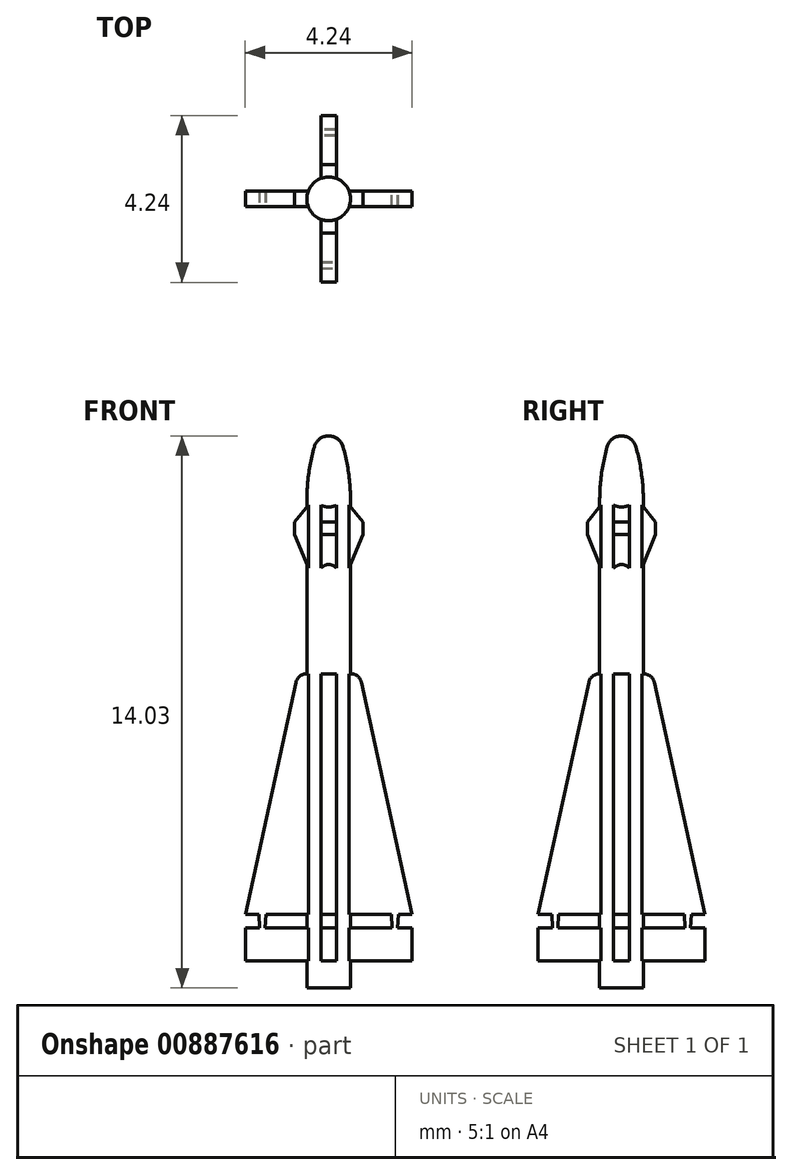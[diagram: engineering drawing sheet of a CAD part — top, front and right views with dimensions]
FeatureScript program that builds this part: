
annotation { "Feature Type Name" : "Feature", "Feature Type Description" : "" }
export const myFeature = defineFeature(function(context is Context, id is Id, definition is map)
    precondition{}
    {
        {
            var Q0;
            Q0=qCreatedBy(makeId("Front.planeOp"),FACE);
            var sketch = newSketch(context, id + "F0", { "sketchPlane" : qUnion([Q0])});
            skLineSegment(sketch, "E0", {"start": v(0, 0) * mm, "end": v(0, 14.03) * mm});
            skLineSegment(sketch, "E1", {"start": v(0.56, 12.36) * mm, "end": v(0.56, 0) * mm});
            skLineSegment(sketch, "E2", {"start": v(0.56, 0) * mm, "end": v(0, 0) * mm});
            skArc(sketch, "E3", {"start": v(0.37, 13.75) * mm, "mid": v(0.23, 13.95) * mm, "end": v(0, 14.03) * mm});
            skArc(sketch, "E4", {"start": v(0.56, 12.36) * mm, "mid": v(0.5, 13.06) * mm, "end": v(0.37, 13.75) * mm});
            skSolve(sketch);
        }
        {
            var Q0;
            {var subQ0=sQuery(id+"F0.wireOp",EDGE,"mrwio9nY-PsAZ-Zbfy-NhIU-sYq0QVbgGXAG");Q0=makeQuery(id+"F0.imprint","IMPRINT",FACE,{"disambiguationData":[TD([[makeQuery(id+"F0.imprint","IMPRINT",EDGE,{"derivedFrom":subQ0}),-1.0]])]});}
            var Q1;
            {var subQ7=sQuery(id+"F0.wireOp",EDGE,"E0");Q1=makeQuery(id+"F0.imprint","IMPRINT",FACE,{"disambiguationData":[TD([[makeQuery(id+"F0.imprint","IMPRINT",EDGE,{"derivedFrom":subQ7}),-1.0]])]});}
            var Q2;
            Q2=sQuery(id+"F0.wireOp",EDGE,"E0");
            revolve(context, id + "F1", {"surfaceOperationType" : NewSurfaceOperationType.NEW, "entities" : qUnion([Q0, Q1]), "axis" : qUnion([Q2]), "revolveType" : RevolveType.FULL});
        }
        {
            var Q0;
            Q0=qCreatedBy(makeId("Front.planeOp"),FACE);
            var sketch = newSketch(context, id + "F2", { "sketchPlane" : qUnion([Q0])});
            skLineSegment(sketch, "E5", {"start": v(0, 0) * mm, "end": v(0, 12.66) * mm});
            skLineSegment(sketch, "E6", {"start": v(0.4, 1.88) * mm, "end": v(0.4, 1.53) * mm});
            skLineSegment(sketch, "E7", {"start": v(0.4, 1.53) * mm, "end": v(2.12, 1.53) * mm});
            skLineSegment(sketch, "E8", {"start": v(0.56, 0) * mm, "end": v(0.56, 32.87) * mm, "construction": true});
            skLineSegment(sketch, "E9", {"start": v(0.4, 1.88) * mm, "end": v(2.12, 1.88) * mm});
            skLineSegment(sketch, "E10", {"start": v(2.12, 1.87) * mm, "end": v(0.83, 7.76) * mm});
            skPoint(sketch, "E11", {"position": v(0.56, 1.88) * mm});
            skLineSegment(sketch, "E12", {"start": v(0, 0.7) * mm, "end": v(2.12, 0.7) * mm});
            skLineSegment(sketch, "E13", {"start": v(2.12, 0.7) * mm, "end": v(2.12, 1.53) * mm});
            skLineSegment(sketch, "E14", {"start": v(0.2, 7.99) * mm, "end": v(0.2, 9.9) * mm});
            skLineSegment(sketch, "E15", {"start": v(0.2, 9.9) * mm, "end": v(0.87, 11.53) * mm});
            skLineSegment(sketch, "E16", {"start": v(0.87, 11.53) * mm, "end": v(0.87, 11.84) * mm});
            skLineSegment(sketch, "E17", {"start": v(0.87, 11.84) * mm, "end": v(0.2, 12.66) * mm});
            skLineSegment(sketch, "E18", {"start": v(0.2, 7.99) * mm, "end": v(0.56, 7.99) * mm});
            skArc(sketch, "E19", {"start": v(0.83, 7.76) * mm, "mid": v(0.73, 7.92) * mm, "end": v(0.56, 7.99) * mm});
            skLineSegment(sketch, "E20", {"start": v(1.6, 1.88) * mm, "end": v(1.61, 1.53) * mm});
            skLineSegment(sketch, "E21", {"start": v(1.77, 1.88) * mm, "end": v(1.75, 1.53) * mm});
            skPoint(sketch, "E22", {"position": v(0.56, 10.76) * mm});
            skPoint(sketch, "E23", {"position": v(0.56, 12.22) * mm});
            skLineSegment(sketch, "E24", {"start": v(0.2, 12.66) * mm, "end": v(0, 12.66) * mm});
            skLineSegment(sketch, "E25.0.0", {"start": v(0.56, 0) * mm, "end": v(-0.56, 0) * mm});
            skSolve(sketch);
        }
        {
            var Q0;
            Q0=qSketchRegion(id+"F2",true);
            extrude(context, id + "F3", {"entities" : qUnion([Q0]), "operationType" : NewBodyOperationType.ADD, "depth" : .4 * mm, "offsetDistance" : 25 * mm, "symmetric" : true});
        }
        {
            var Q0;
            Q0=makeQuery(id+"F1.opRevolve","SWEPT_BODY",BODY,{"disambiguationData":[OSD([sQuery(id+"F0.wireOp",EDGE,"E0"),sQuery(id+"F0.wireOp",EDGE,"E1"),sQuery(id+"F0.wireOp",EDGE,"E2"),sQuery(id+"F0.wireOp",EDGE,"2EiOItwe-9FNA-eY8p-DkXH-AMy5AHyUmzZA"),sQuery(id+"F0.wireOp",EDGE,"lF35QjYl-MEgV-fRWE-0Yr6-Bt5vS8A7brRf")])]});
            var Q1;
            Q1=makeQuery(id+"F1.opRevolve","SWEPT_FACE",FACE,{"disambiguationData":[OSD([sQuery(id+"F0.wireOp",EDGE,"E1")])]});
            circularPattern(context, id + "F4", {"operationType" : NewBodyOperationType.ADD, "entities" : qUnion([Q0]), "axis" : qUnion([Q1]), "angle" : 360 * degree, "instanceCount" : 4, "equalSpace" : true, "computeTransformsWithoutBuiltin" : true});
        }
    });
